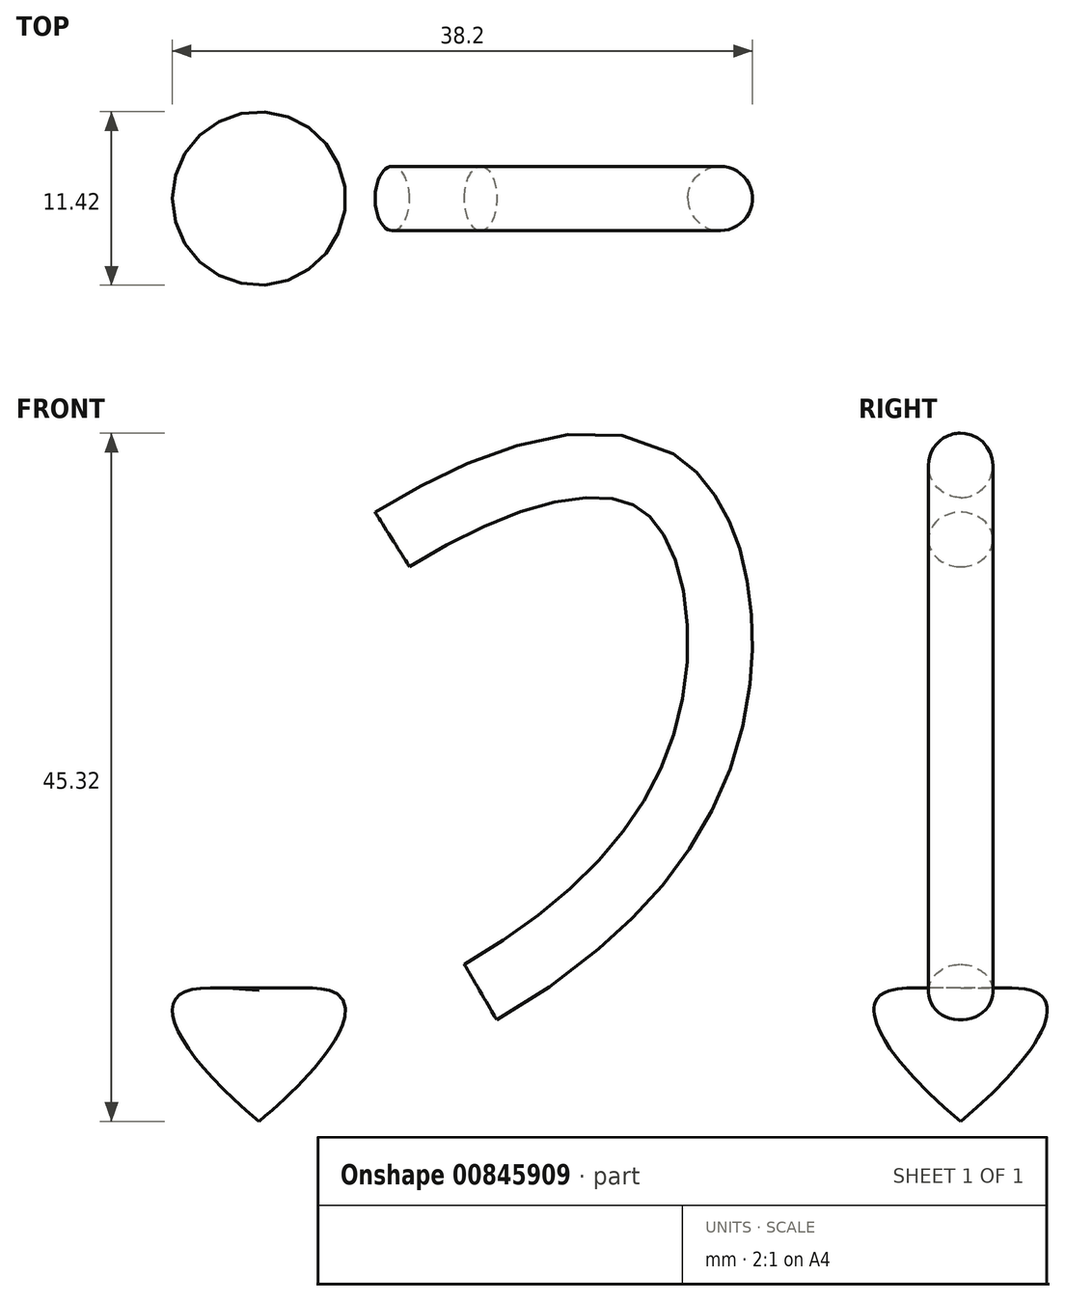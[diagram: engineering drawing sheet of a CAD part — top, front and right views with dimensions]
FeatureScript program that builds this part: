
annotation { "Feature Type Name" : "Feature", "Feature Type Description" : "" }
export const myFeature = defineFeature(function(context is Context, id is Id, definition is map)
    precondition{}
    {
        {
            var Q0;
            Q0=qCreatedBy(makeId("Front.planeOp"),FACE);
            var sketch = newSketch(context, id + "F0", { "sketchPlane" : qUnion([Q0])});
            skFitSpline(sketch, "E0", {"points": [v(0, 0) * mm, v(23.05, -7.73) * mm, v(10.45, 41.66) * mm, v(18.66, 56.08) * mm, v(24.03, 61.1) * mm, v(2.4, 46.57) * mm, v(8.84, 9.63) * mm, v(-4.92, 8.52) * mm, v(0, 0) * mm]});
            skLineSegment(sketch, "E1", {"start": v(0, 67.17) * mm, "end": v(0, -42.83) * mm});
            skSolve(sketch);
        }
        {
            var Q0;
            {var subQ0=sQuery(id+"F0.wireOp",EDGE,"E1");var subQ1=sQuery(id+"F0.wireOp",EDGE,"E0");var subQ2=makeQuery(id+"F0.imprint","INTERSECT",VERTEX,{"disambiguationData":[OD(0.0)],"derivedFrom":[subQ1,subQ0]});Q0=makeQuery(id+"F0.imprint","IMPRINT",FACE,{"disambiguationData":[TD([[makeQuery(id+"F0.imprint","IMPRINT",EDGE,{"disambiguationData":[TD([[subQ2,-1.0]])],"derivedFrom":subQ1}),1.0]])]});}
            var Q1;
            Q1=sQuery(id+"F0.wireOp",EDGE,"E1");
            revolve(context, id + "F1", {"surfaceOperationType" : NewSurfaceOperationType.NEW, "entities" : qUnion([Q0]), "axis" : qUnion([Q1]), "revolveType" : RevolveType.FULL});
        }
        {
            var Q0;
            Q0=qCreatedBy(makeId("Front.planeOp"),FACE);
            var sketch = newSketch(context, id + "F2", { "sketchPlane" : qUnion([Q0])});
            skFitSpline(sketch, "E2", {"points": [v(8.85, 38.2) * mm, v(26.23, 41.96) * mm, v(29.54, 26.03) * mm, v(14.53, 8.62) * mm], "startDerivative": vector(57.84, 36.47) * mm, "endDerivative": vector(-62.92, -36.65) * mm});
            skSolve(sketch);
        }
        {
            var Q0;
            Q0=sQuery(id+"F2.wireOp",EDGE,"E2");
            var Q1;
            Q1=sQuery(id+"F2.wireOp",VERTEX,"E2.end");
            cPlane(context, id + "F3", {"entities" : qUnion([Q0, Q1]), "cplaneType" : CPlaneType.CURVE_POINT, "offset" : 25.4 * mm, "width" : 152.4 * mm, "height" : 152.4 * mm});
        }
        {
            var Q0;
            Q0=qCreatedBy(id+"F3.planeOp",FACE);
            var sketch = newSketch(context, id + "F4", { "sketchPlane" : qUnion([Q0])});
            skCircle(sketch, "E3", {"center": v(0, 0) * mm, "radius": 2.12 * mm});
            skSolve(sketch);
        }
        {
            var Q0;
            Q0=makeQuery(id+"F4.imprint","IMPRINT",FACE,{"disambiguationData":[TD([[makeQuery(id+"F4.imprint","IMPRINT",EDGE,{"derivedFrom":sQuery(id+"F4.wireOp",EDGE,"E3")}),1.0]])]});
            var Q1;
            Q1=sQuery(id+"F4.wireOp",EDGE,"E3");
            var Q2;
            Q2=sQuery(id+"F2.wireOp",EDGE,"E2");
            sweep(context, id + "F5", {"operationType" : NewBodyOperationType.ADD, "profiles" : qUnion([Q0]), "surfaceOperationType" : NewSurfaceOperationType.ADD, "surfaceProfiles" : qUnion([Q1]), "path" : qUnion([Q2])});
        }
    });
